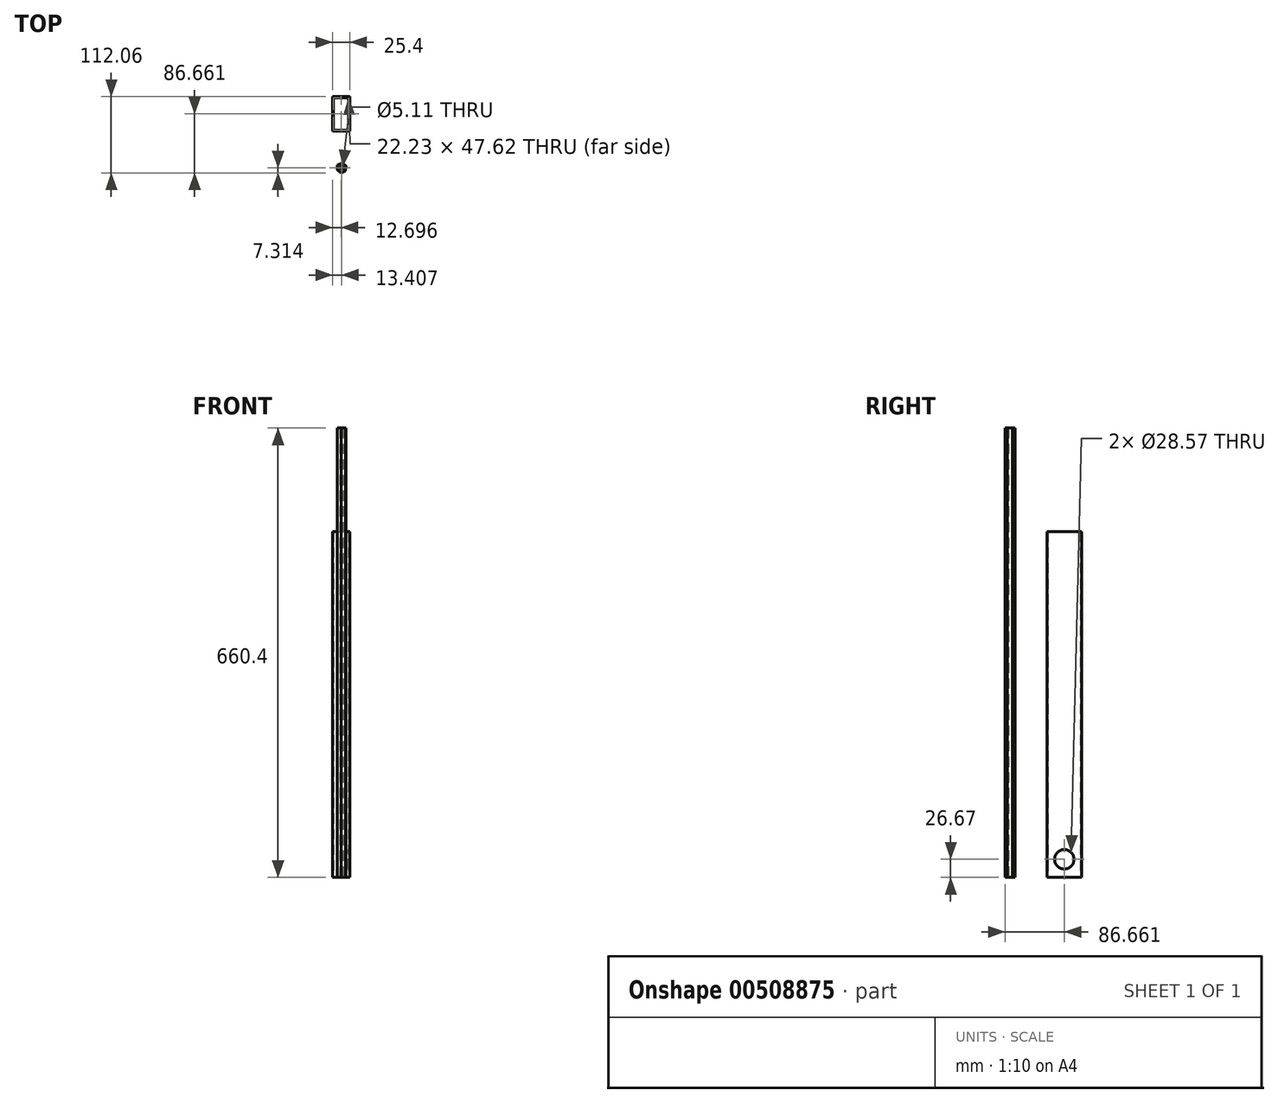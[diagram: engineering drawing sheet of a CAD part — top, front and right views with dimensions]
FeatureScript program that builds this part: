
annotation { "Feature Type Name" : "Feature", "Feature Type Description" : "" }
export const myFeature = defineFeature(function(context is Context, id is Id, definition is map)
    precondition{}
    {
        {
            var Q0;
            Q0=qCreatedBy(makeId("Top.planeOp"),FACE);
            var sketch = newSketch(context, id + "F0", { "sketchPlane" : qUnion([Q0])});
            skLineSegment(sketch, "E0.bottom", {"start": v(-62.95, 81.54) * mm, "end": v(-37.55, 81.54) * mm});
            skLineSegment(sketch, "E0.top", {"start": v(-62.95, 30.74) * mm, "end": v(-37.55, 30.74) * mm});
            skLineSegment(sketch, "E0.left", {"start": v(-62.95, 81.54) * mm, "end": v(-62.95, 30.74) * mm});
            skLineSegment(sketch, "E0.right", {"start": v(-37.55, 81.54) * mm, "end": v(-37.55, 30.74) * mm});
            skPoint(sketch, "E0.middle", {"position": v(-50.25, 56.14) * mm});
            skLineSegment(sketch, "E1.bottom", {"start": v(-61.37, 79.95) * mm, "end": v(-39.14, 79.95) * mm});
            skLineSegment(sketch, "E1.top", {"start": v(-61.37, 32.33) * mm, "end": v(-39.14, 32.33) * mm});
            skLineSegment(sketch, "E1.left", {"start": v(-61.37, 79.95) * mm, "end": v(-61.37, 32.33) * mm});
            skLineSegment(sketch, "E1.right", {"start": v(-39.14, 79.95) * mm, "end": v(-39.14, 32.33) * mm});
            skSolve(sketch);
        }
        {
            var Q0;
            Q0=qSketchRegion(id+"F0",true);
            extrude(context, id + "F1", {"entities" : qUnion([Q0]), "depth" : 508 * mm});
        }
        {
            var Q0;
            Q0=makeQuery(id+"F1.opExtrude","SWEPT_FACE",FACE,{"disambiguationData":[OSD([sQuery(id+"F0.wireOp",EDGE,"E0.left")])]});
            var sketch = newSketch(context, id + "F2", { "sketchPlane" : qUnion([Q0])});
            skLineSegment(sketch, "E2.0.0", {"start": v(-81.54, 0) * mm, "end": v(-30.74, 0) * mm});
            skLineSegment(sketch, "E2.0.1", {"start": v(-30.74, 0) * mm, "end": v(-30.74, 508) * mm});
            skLineSegment(sketch, "E2.0.2", {"start": v(-30.74, 508) * mm, "end": v(-81.54, 508) * mm});
            skLineSegment(sketch, "E2.0.3", {"start": v(-81.54, 508) * mm, "end": v(-81.54, 0) * mm});
            skCircle(sketch, "E3", {"center": v(-56.14, 26.67) * mm, "radius": 14.29 * mm});
            skPoint(sketch, "E3.centerSnap0", {"position": v(-56.14, 0) * mm});
            skSolve(sketch);
        }
        {
            var Q0;
            Q0=makeQuery(id+"F2.imprint","IMPRINT",FACE,{"disambiguationData":[TD([[makeQuery(id+"F2.imprint","IMPRINT",EDGE,{"derivedFrom":sQuery(id+"F2.wireOp",EDGE,"E3")}),1.0]])]});
            var Q1;
            Q1=makeQuery(id+"F1.opExtrude","SWEPT_FACE",FACE,{"disambiguationData":[OSD([sQuery(id+"F0.wireOp",EDGE,"E0.right")])]});
            extrude(context, id + "F3", {"entities" : qUnion([Q0]), "operationType" : NewBodyOperationType.REMOVE, "endBound" : BoundingType.UP_TO_SURFACE, "oppositeDirection" : true, "endBoundEntityFace" : qUnion([Q1]), "depth" : 25.4 * mm});
        }
        {
            var Q0;
            Q0=qCreatedBy(makeId("Top.planeOp"),FACE);
            var sketch = newSketch(context, id + "F4", { "sketchPlane" : qUnion([Q0])});
            skCircle(sketch, "E4", {"center": v(-49.54, -23.2) * mm, "radius": 2.55 * mm});
            skCircle(sketch, "E5.cCircle", {"center": v(-49.54, -23.2) * mm, "radius": 6.35 * mm, "construction": true});
            skLineSegment(sketch, "E5.0", {"start": v(-43.5, -27.36) * mm, "end": v(-50.12, -30.52) * mm});
            skLineSegment(sketch, "E5.1", {"start": v(-50.12, -30.52) * mm, "end": v(-56.16, -26.36) * mm});
            skLineSegment(sketch, "E5.2", {"start": v(-56.16, -26.36) * mm, "end": v(-55.58, -19.05) * mm});
            skLineSegment(sketch, "E5.3", {"start": v(-55.58, -19.05) * mm, "end": v(-48.96, -15.9) * mm});
            skLineSegment(sketch, "E5.4", {"start": v(-48.96, -15.9) * mm, "end": v(-42.92, -20.05) * mm});
            skLineSegment(sketch, "E5.5", {"start": v(-42.92, -20.05) * mm, "end": v(-43.5, -27.36) * mm});
            skPoint(sketch, "E5.0.midPoint", {"position": v(-46.81, -28.94) * mm});
            skSolve(sketch);
        }
        {
            var Q0;
            Q0=makeQuery(id+"F4.imprint","IMPRINT",FACE,{"disambiguationData":[TD([[makeQuery(id+"F4.imprint","IMPRINT",EDGE,{"derivedFrom":sQuery(id+"F4.wireOp",EDGE,"E4")}),-1.0]])]});
            extrude(context, id + "F5", {"entities" : qUnion([Q0]), "depth" : 660.4 * mm});
        }
    });
